FCSTD DOCUMENT  (FreeCAD 1.0R39109 (Git))
Label: 10_shelf_top_assembly
License: All rights reserved
LicenseURL: http://en.wikipedia.org/wiki/All_rights_reserved
objects: App::FeaturePython×25, TechDraw::DrawViewDimension×11, App::Link×9, TechDraw::DrawProjGroupItem×5, Assembly::JointGroup×1, Assembly::AssemblyObject×1, TechDraw::DrawSVGTemplate×1, TechDraw::DrawProjGroup×1, TechDraw::DrawPage×1
note: 17 computed .brp shape members not serialized (recipe doc carries the construction recipe); baked Part::Feature solids carry a one-line shape summary decoded from their .brp
EXTERNAL_REF file=12_shelf_top_down.FCStd obj=Body
EXTERNAL_REF file=13_shelf_sides_and_middle.FCStd obj=Body
EXTERNAL_REF file=14_shelf_trays.FCStd obj=Body

FEATURE [App::Link] Body
  LinkedObject = -> <external 12_shelf_top_down.FCStd>#Body
FEATURE [App::FeaturePython] GroundedJoint  # Assembly grounded joint (typed FeaturePython)
  ObjectToGround = -> Body
FEATURE [App::Link] Body001
  LinkPlacement = pos=(-4.124e-13,4.349e-13,900) rot=(0,1,0;3.14159rad)
  LinkedObject = -> <external 12_shelf_top_down.FCStd>#Body
  Placement = pos=(-4.124e-13,4.349e-13,900) rot=(0,1,0;3.14159rad)
FEATURE [App::Link] Body002
  LinkPlacement = pos=(-597,2.282e-13,450) rot=(0,1,0;4.71239rad)
  LinkedObject = -> <external 13_shelf_sides_and_middle.FCStd>#Body
  Placement = pos=(-597,2.282e-13,450) rot=(0,1,0;4.71239rad)
FEATURE [App::Link] Body003
  LinkPlacement = pos=(615,9.28e-14,450) rot=(0,1,0;4.71239rad)
  LinkedObject = -> <external 13_shelf_sides_and_middle.FCStd>#Body
  Placement = pos=(615,9.28e-14,450) rot=(0,1,0;4.71239rad)
FEATURE [App::Link] Body004
  LinkPlacement = pos=(-9,1.041e-13,450) rot=(0,1,0;1.5708rad)
  LinkedObject = -> <external 13_shelf_sides_and_middle.FCStd>#Body
  Placement = pos=(-9,1.041e-13,450) rot=(0,1,0;1.5708rad)
FEATURE [App::FeaturePython] Joint  label="Distance"  # Assembly joint (typed FeaturePython)
  Activated = true
  AngleMax = 0
  AngleMin = 0
  Detach1 = false
  Detach2 = false
  Distance = 0
  Distance2 = 0
  EnableAngleMax = false
  EnableAngleMin = false
  EnableLengthMax = false
  EnableLengthMin = false
  JointType = 5 (Distance)
  LengthMax = 0
  LengthMin = 0
  Placement1 = pos=(-432,4e-16,9) rot=(0.57735,0.57735,-0.57735;4.18879rad)
  Placement2 = pos=(-4e-15,-5.5e-15,18) rot=(0,0,1;0rad)
  Reference1 = -> Assembly [Body002.Face4,Body002.Face4]
  Reference2 = -> Assembly [Body.Face6,Body.Vertex8]
FEATURE [App::FeaturePython] Joint001  label="Distance001"  # Assembly joint (typed FeaturePython)
  Activated = true
  AngleMax = 0
  AngleMin = 0
  Detach1 = false
  Detach2 = false
  Distance = 0
  Distance2 = 0
  EnableAngleMax = false
  EnableAngleMin = false
  EnableLengthMax = false
  EnableLengthMin = false
  JointType = 5 (Distance)
  LengthMax = 0
  LengthMin = 0
  Placement1 = pos=(0,-2.6e-15,18) rot=(0,0,1;0rad)
  Placement2 = pos=(-615,1.3e-15,9) rot=(-0.57735,-0.57735,0.57735;2.0944rad)
  Reference1 = -> Assembly [Body002.Face6,Body002.Vertex2]
  Reference2 = -> Assembly [Body.Face4,Body.Face4]
FEATURE [App::FeaturePython] Joint002  label="Distance002"  # Assembly joint (typed FeaturePython)
  Activated = true
  AngleMax = 0
  AngleMin = 0
  Detach1 = false
  Detach2 = false
  Distance = 0
  Distance2 = 0
  EnableAngleMax = false
  EnableAngleMin = false
  EnableLengthMax = false
  EnableLengthMin = false
  JointType = 5 (Distance)
  LengthMax = 0
  LengthMin = 0
  Placement1 = pos=(0,87.5,9) rot=(-1,0,0;1.5708rad)
  Placement2 = pos=(6.2e-15,87.5,9) rot=(-1,0,0;1.5708rad)
  Reference1 = -> Assembly [Body002.Face1,Body002.Vertex1]
  Reference2 = -> Assembly [Body.Face1,Body.Vertex1]
FEATURE [App::FeaturePython] Joint003  label="Distance003"  # Assembly joint (typed FeaturePython)
  Activated = true
  AngleMax = 0
  AngleMin = 0
  Detach1 = false
  Detach2 = false
  Distance = 0
  Distance2 = 0
  EnableAngleMax = false
  EnableAngleMin = false
  EnableLengthMax = false
  EnableLengthMin = false
  JointType = 5 (Distance)
  LengthMax = 0
  LengthMin = 0
  Placement1 = pos=(-432,-1.2e-15,9) rot=(0.57735,0.57735,-0.57735;4.18879rad)
  Placement2 = pos=(-4e-15,-5.5e-15,18) rot=(0,0,1;0rad)
  Reference1 = -> Assembly [Body003.Face4,Body003.Face4]
  Reference2 = -> Assembly [Body.Face6,Body.Vertex4]
FEATURE [App::FeaturePython] Joint004  label="Distance004"  # Assembly joint (typed FeaturePython)
  Activated = true
  AngleMax = 0
  AngleMin = 0
  Detach1 = false
  Detach2 = false
  Distance = 0
  Distance2 = 0
  EnableAngleMax = false
  EnableAngleMin = false
  EnableLengthMax = false
  EnableLengthMin = false
  JointType = 5 (Distance)
  LengthMax = 0
  LengthMin = 0
  Placement1 = pos=(0,-87.5,9) rot=(0,-0.707107,0.707107;3.14159rad)
  Placement2 = pos=(-6.2e-15,-87.5,9) rot=(0,-0.707107,0.707107;3.14159rad)
  Reference1 = -> Assembly [Body003.Face3,Body003.Vertex8]
  Reference2 = -> Assembly [Body.Face3,Body.Vertex5]
FEATURE [App::FeaturePython] Joint005  label="Distance005"  # Assembly joint (typed FeaturePython)
  Activated = true
  AngleMax = 0
  AngleMin = 0
  Detach1 = false
  Detach2 = false
  Distance = 0
  Distance2 = 0
  EnableAngleMax = false
  EnableAngleMin = false
  EnableLengthMax = false
  EnableLengthMin = false
  JointType = 5 (Distance)
  LengthMax = 0
  LengthMin = 0
  Placement1 = pos=(0,-6.3e-15,0) rot=(0,0,1;0rad)
  Placement2 = pos=(615,-1.3e-15,9) rot=(0.57735,-0.57735,0.57735;4.18879rad)
  Reference1 = -> Assembly [Body003.Face5,Body003.Vertex7]
  Reference2 = -> Assembly [Body.Face2,Body.Face2]
FEATURE [App::FeaturePython] Joint006  label="Distance006"  # Assembly joint (typed FeaturePython)
  Activated = true
  AngleMax = 0
  AngleMin = 0
  Detach1 = false
  Detach2 = false
  Distance = 0
  Distance2 = 0
  EnableAngleMax = false
  EnableAngleMin = false
  EnableLengthMax = false
  EnableLengthMin = false
  JointType = 5 (Distance)
  LengthMax = 0
  LengthMin = 0
  Placement1 = pos=(432,-1.5e-15,9) rot=(-0.57735,0.57735,-0.57735;2.0944rad)
  Placement2 = pos=(-4e-15,-5.5e-15,18) rot=(0,0,1;0rad)
  Reference1 = -> Assembly [Body004.Face2,Body004.Face2]
  Reference2 = -> Assembly [Body.Face6,Body.Vertex4]
FEATURE [App::FeaturePython] Joint007  label="Distance007"  # Assembly joint (typed FeaturePython)
  Activated = true
  AngleMax = 0
  AngleMin = 0
  Detach1 = false
  Detach2 = false
  Distance = 0
  Distance2 = 0
  EnableAngleMax = false
  EnableAngleMin = false
  EnableLengthMax = false
  EnableLengthMin = false
  JointType = 5 (Distance)
  LengthMax = 0
  LengthMin = 0
  Placement1 = pos=(0,-87.5,9) rot=(0,-0.707107,0.707107;3.14159rad)
  Placement2 = pos=(-6.2e-15,-87.5,9) rot=(0,-0.707107,0.707107;3.14159rad)
  Reference1 = -> Assembly [Body004.Face3,Body004.Vertex6]
  Reference2 = -> Assembly [Body.Face3,Body.Face3]
FEATURE [App::FeaturePython] Joint008  label="Distance008"  # Assembly joint (typed FeaturePython)
  Activated = true
  AngleMax = 0
  AngleMin = 0
  Detach1 = false
  Detach2 = false
  Distance = -588
  Distance2 = 0
  EnableAngleMax = false
  EnableAngleMin = false
  EnableLengthMax = false
  EnableLengthMin = false
  JointType = 5 (Distance)
  LengthMax = 0
  LengthMin = 0
  Placement1 = pos=(0,-2.6e-15,0) rot=(0,0,1;0rad)
  Placement2 = pos=(0,-3.3e-15,0) rot=(0,0,1;0rad)
  Reference1 = -> Assembly [Body002.Face5,Body002.Face5]
  Reference2 = -> Assembly [Body004.Face5,Body004.Face5]
FEATURE [App::FeaturePython] Joint009  label="Distance009"  # Assembly joint (typed FeaturePython)
  Activated = true
  AngleMax = 0
  AngleMin = 0
  Detach1 = false
  Detach2 = false
  Distance = 0
  Distance2 = 0
  EnableAngleMax = false
  EnableAngleMin = false
  EnableLengthMax = false
  EnableLengthMin = false
  JointType = 5 (Distance)
  LengthMax = 0
  LengthMin = 0
  Placement1 = pos=(432,-4e-16,9) rot=(-0.57735,0.57735,-0.57735;2.0944rad)
  Placement2 = pos=(1.04e-14,-3.2e-15,18) rot=(0,0,1;0rad)
  Reference1 = -> Assembly [Body003.Face2,Body003.Vertex5]
  Reference2 = -> Assembly [Body001.Face6,Body001.Face6]
FEATURE [App::FeaturePython] Joint010  label="Distance010"  # Assembly joint (typed FeaturePython)
  Activated = true
  AngleMax = 0
  AngleMin = 0
  Detach1 = false
  Detach2 = false
  Distance = 0
  Distance2 = 0
  EnableAngleMax = false
  EnableAngleMin = false
  EnableLengthMax = false
  EnableLengthMin = false
  JointType = 5 (Distance)
  LengthMax = 0
  LengthMin = 0
  Placement1 = pos=(615,1.5e-15,9) rot=(-0.57735,0.57735,-0.57735;2.0944rad)
  Placement2 = pos=(0,-2.6e-15,18) rot=(0,0,1;0rad)
  Reference1 = -> Assembly [Body001.Face2,Body001.Vertex4]
  Reference2 = -> Assembly [Body002.Face6,Body002.Vertex6]
FEATURE [App::FeaturePython] Joint011  label="Distance011"  # Assembly joint (typed FeaturePython)
  Activated = true
  AngleMax = 0
  AngleMin = 0
  Detach1 = false
  Detach2 = false
  Distance = 0
  Distance2 = 0
  EnableAngleMax = false
  EnableAngleMin = false
  EnableLengthMax = false
  EnableLengthMin = false
  JointType = 5 (Distance)
  LengthMax = 0
  LengthMin = 0
  Placement1 = pos=(-7.8e-15,-87.5,9) rot=(0,-0.707107,0.707107;3.14159rad)
  Placement2 = pos=(0,-87.5,9) rot=(0,-0.707107,0.707107;3.14159rad)
  Reference1 = -> Assembly [Body001.Face3,Body001.Vertex6]
  Reference2 = -> Assembly [Body002.Face3,Body002.Vertex6]
FEATURE [App::Link] Body005
  LinkPlacement = pos=(-303,2.659e-13,294) rot=(0,0,1;3.14159rad)
  LinkedObject = -> <external 14_shelf_trays.FCStd>#Body
  Placement = pos=(-303,2.659e-13,294) rot=(0,0,1;3.14159rad)
FEATURE [App::Link] Body006
  LinkPlacement = pos=(-303,3.633e-13,588) rot=(0,0,1;3.14159rad)
  LinkedObject = -> <external 14_shelf_trays.FCStd>#Body
  Placement = pos=(-303,3.633e-13,588) rot=(0,0,1;3.14159rad)
FEATURE [App::Link] Body007
  LinkPlacement = pos=(303,1.38e-13,294) rot=(0,0,1;3.14159rad)
  LinkedObject = -> <external 14_shelf_trays.FCStd>#Body
  Placement = pos=(303,1.38e-13,294) rot=(0,0,1;3.14159rad)
FEATURE [App::Link] Body008
  LinkPlacement = pos=(303,2.92e-13,588) rot=(0,0,1;3.14159rad)
  LinkedObject = -> <external 14_shelf_trays.FCStd>#Body
  Placement = pos=(303,2.92e-13,588) rot=(0,0,1;3.14159rad)
FEATURE [App::FeaturePython] Joint012  label="Tray1"  # Assembly joint (typed FeaturePython)
  Activated = true
  AngleMax = 0
  AngleMin = 0
  Detach1 = false
  Detach2 = false
  Distance = 276
  Distance2 = 0
  EnableAngleMax = false
  EnableAngleMin = false
  EnableLengthMax = false
  EnableLengthMin = false
  JointType = 5 (Distance)
  LengthMax = 0
  LengthMin = 0
  Placement1 = pos=(0,-3.8e-15,18) rot=(0,0,1;0rad)
  Placement2 = pos=(1.04e-14,-3.2e-15,18) rot=(0,0,1;0rad)
  Reference1 = -> Assembly [Body008.Face6,Body008.Face6]
  Reference2 = -> Assembly [Body001.Face6,Body001.Vertex4]
FEATURE [App::FeaturePython] Joint013  label="Distance013"  # Assembly joint (typed FeaturePython)
  Activated = true
  AngleMax = 0
  AngleMin = 0
  Detach1 = false
  Detach2 = false
  Distance = 0
  Distance2 = 0
  EnableAngleMax = false
  EnableAngleMin = false
  EnableLengthMax = false
  EnableLengthMin = false
  JointType = 5 (Distance)
  LengthMax = 0
  LengthMin = 0
  Placement1 = pos=(0,-6.3e-15,18) rot=(0,0,1;0rad)
  Placement2 = pos=(-294,2.2e-15,9) rot=(-0.57735,-0.57735,0.57735;2.0944rad)
  Reference1 = -> Assembly [Body003.Face6,Body003.Vertex6]
  Reference2 = -> Assembly [Body008.Face4,Body008.Vertex1]
FEATURE [App::FeaturePython] Joint014  label="Distance014"  # Assembly joint (typed FeaturePython)
  Activated = true
  AngleMax = 0
  AngleMin = 0
  Detach1 = false
  Detach2 = false
  Distance = 0
  Distance2 = 0
  EnableAngleMax = false
  EnableAngleMin = false
  EnableLengthMax = false
  EnableLengthMin = false
  JointType = 5 (Distance)
  LengthMax = 0
  LengthMin = 0
  Placement1 = pos=(-7.8e-15,-87.5,9) rot=(0,-0.707107,0.707107;3.14159rad)
  Placement2 = pos=(0,87.5,9) rot=(-1,0,0;1.5708rad)
  Reference1 = -> Assembly [Body001.Face3,Body001.Vertex8]
  Reference2 = -> Assembly [Body008.Face1,Body008.Face1]
FEATURE [App::FeaturePython] Joint015  label="Tray2"  # Assembly joint (typed FeaturePython)
  Activated = true
  AngleMax = 0
  AngleMin = 0
  Detach1 = false
  Detach2 = false
  Distance = 276
  Distance2 = 0
  EnableAngleMax = false
  EnableAngleMin = false
  EnableLengthMax = false
  EnableLengthMin = false
  JointType = 5 (Distance)
  LengthMax = 0
  LengthMin = 0
  Placement1 = pos=(0,-3.9e-15,18) rot=(0,0,1;0rad)
  Placement2 = pos=(0,-3.8e-15,0) rot=(0,0,1;0rad)
  Reference1 = -> Assembly [Body007.Face6,Body007.Face6]
  Reference2 = -> Assembly [Body008.Face5,Body008.Vertex5]
FEATURE [App::FeaturePython] Joint016  label="Distance016"  # Assembly joint (typed FeaturePython)
  Activated = true
  AngleMax = 0
  AngleMin = 0
  Detach1 = false
  Detach2 = false
  Distance = 0
  Distance2 = 0
  EnableAngleMax = false
  EnableAngleMin = false
  EnableLengthMax = false
  EnableLengthMin = false
  JointType = 5 (Distance)
  LengthMax = 0
  LengthMin = 0
  Placement1 = pos=(-294,1e-15,9) rot=(-0.57735,-0.57735,0.57735;2.0944rad)
  Placement2 = pos=(0,-6.3e-15,18) rot=(0,0,1;0rad)
  Reference1 = -> Assembly [Body007.Face4,Body007.Vertex2]
  Reference2 = -> Assembly [Body003.Face6,Body003.Face6]
FEATURE [App::FeaturePython] Joint017  label="Distance017"  # Assembly joint (typed FeaturePython)
  Activated = true
  AngleMax = 0
  AngleMin = 0
  Detach1 = false
  Detach2 = false
  Distance = 0
  Distance2 = 0
  EnableAngleMax = false
  EnableAngleMin = false
  EnableLengthMax = false
  EnableLengthMin = false
  JointType = 5 (Distance)
  LengthMax = 0
  LengthMin = 0
  Placement1 = pos=(0,87.5,9) rot=(-1,0,0;1.5708rad)
  Placement2 = pos=(0,-87.5,9) rot=(0,-0.707107,0.707107;3.14159rad)
  Reference1 = -> Assembly [Body007.Face1,Body007.Vertex2]
  Reference2 = -> Assembly [Body003.Face3,Body003.Face3]
FEATURE [App::FeaturePython] Joint018  label="tray3"  # Assembly joint (typed FeaturePython)
  Activated = true
  AngleMax = 0
  AngleMin = 0
  Detach1 = false
  Detach2 = false
  Distance = 276
  Distance2 = 0
  EnableAngleMax = false
  EnableAngleMin = false
  EnableLengthMax = false
  EnableLengthMin = false
  JointType = 5 (Distance)
  LengthMax = 0
  LengthMin = 0
  Placement1 = pos=(0,2.4e-15,18) rot=(0,0,1;0rad)
  Placement2 = pos=(1.04e-14,-3.2e-15,18) rot=(0,0,1;0rad)
  Reference1 = -> Assembly [Body006.Face6,Body006.Vertex2]
  Reference2 = -> Assembly [Body001.Face6,Body001.Face6]
FEATURE [App::FeaturePython] Joint019  label="Distance019"  # Assembly joint (typed FeaturePython)
  Activated = true
  AngleMax = 0
  AngleMin = 0
  Detach1 = false
  Detach2 = false
  Distance = 0
  Distance2 = 0
  EnableAngleMax = false
  EnableAngleMin = false
  EnableLengthMax = false
  EnableLengthMin = false
  JointType = 5 (Distance)
  LengthMax = 0
  LengthMin = 0
  Placement1 = pos=(0,87.5,9) rot=(-1,0,0;1.5708rad)
  Placement2 = pos=(-7.8e-15,-87.5,9) rot=(0,-0.707107,0.707107;3.14159rad)
  Reference1 = -> Assembly [Body006.Face1,Body006.Vertex4]
  Reference2 = -> Assembly [Body001.Face3,Body001.Face3]
FEATURE [App::FeaturePython] Joint020  label="Distance020"  # Assembly joint (typed FeaturePython)
  Activated = true
  AngleMax = 0
  AngleMin = 0
  Detach1 = false
  Detach2 = false
  Distance = 0
  Distance2 = 0
  EnableAngleMax = false
  EnableAngleMin = false
  EnableLengthMax = false
  EnableLengthMin = false
  JointType = 5 (Distance)
  LengthMax = 0
  LengthMin = 0
  Placement1 = pos=(0,-2.6e-15,0) rot=(0,0,1;0rad)
  Placement2 = pos=(294,1.1e-15,9) rot=(-0.57735,0.57735,-0.57735;2.0944rad)
  Reference1 = -> Assembly [Body002.Face5,Body002.Vertex3]
  Reference2 = -> Assembly [Body006.Face2,Body006.Face2]
FEATURE [App::FeaturePython] Joint021  label="tray4"  # Assembly joint (typed FeaturePython)
  Activated = true
  AngleMax = 0
  AngleMin = 0
  Detach1 = false
  Detach2 = false
  Distance = 276
  Distance2 = 0
  EnableAngleMax = false
  EnableAngleMin = false
  EnableLengthMax = false
  EnableLengthMin = false
  JointType = 5 (Distance)
  LengthMax = 0
  LengthMin = 0
  Placement1 = pos=(0,-4.5e-15,18) rot=(0,0,1;0rad)
  Placement2 = pos=(0,-5.2e-15,0) rot=(0,0,1;0rad)
  Reference1 = -> Assembly [Body005.Face6,Body005.Face6]
  Reference2 = -> Assembly [Body006.Face5,Body006.Face5]
FEATURE [App::FeaturePython] Joint022  label="Distance021"  # Assembly joint (typed FeaturePython)
  Activated = true
  AngleMax = 0
  AngleMin = 0
  Detach1 = false
  Detach2 = false
  Distance = 0
  Distance2 = 0
  EnableAngleMax = false
  EnableAngleMin = false
  EnableLengthMax = false
  EnableLengthMin = false
  JointType = 5 (Distance)
  LengthMax = 0
  LengthMin = 0
  Placement1 = pos=(0,-87.5,9) rot=(0,-0.707107,0.707107;3.14159rad)
  Placement2 = pos=(0,87.5,9) rot=(-1,0,0;1.5708rad)
  Reference1 = -> Assembly [Body002.Face3,Body002.Face3]
  Reference2 = -> Assembly [Body005.Face1,Body005.Vertex4]
FEATURE [App::FeaturePython] Joint023  label="Distance022"  # Assembly joint (typed FeaturePython)
  Activated = true
  AngleMax = 0
  AngleMin = 0
  Detach1 = false
  Detach2 = false
  Distance = 0
  Distance2 = 0
  EnableAngleMax = false
  EnableAngleMin = false
  EnableLengthMax = false
  EnableLengthMin = false
  JointType = 5 (Distance)
  LengthMax = 0
  LengthMin = 0
  Placement1 = pos=(294,9e-16,9) rot=(-0.57735,0.57735,-0.57735;2.0944rad)
  Placement2 = pos=(0,-2.6e-15,0) rot=(0,0,1;0rad)
  Reference1 = -> Assembly [Body005.Face2,Body005.Vertex3]
  Reference2 = -> Assembly [Body002.Face5,Body002.Face5]
FEATURE [Assembly::JointGroup] Joints
  Group = -> [GroundedJoint,Joint,Joint001,Joint002,Joint003,Joint004,Joint005,Joint006,Joint007,Joint008,Joint009,Joint010,Joint011,Joint012,Joint013,Joint014,Joint015,Joint016,Joint017,Joint018,Joint019,Joint020,Joint021,Joint022,Joint023]
FEATURE [Assembly::AssemblyObject] Assembly
  Group = -> [Joints,Body,GroundedJoint,Body001,Body002,Body003,Body004,Joint,Joint001,Joint002,Joint003,Joint004,Joint005,Joint006,Joint007,Joint008,Joint009,Joint010,Joint011,Body005,Body006,Body007,Body008,Joint012,Joint013,Joint014,Joint015,Joint016,Joint017,Joint018,Joint019,Joint020,Joint021,Joint022,Joint023]
  Origin = -> Origin
  Type = Assembly
FEATURE [TechDraw::DrawSVGTemplate] Template
  EditableTexts = AuthorName=Matthias Mosimann; CheckDate=CHECK DATE; CreationDate=21/07/2025; DrawingNumber=NUMBER; FC-Scale=1 : 10; FC-Title=Regal oben; SheetNumber=1/2; Subtitle=Alle Dicken 18mm Buche keilverzinkt; SupervisorName=SUPERVISOR NAME; Weight=N/A
  Height = 297
  Orientation = 1
  Template = C:/Program Files/FreeCAD 1.0/data/Mod/TechDraw/Templates/A3_Landscape_TD.svg
  Width = 420
FEATURE [TechDraw::DrawProjGroupItem] View  label="Front"
  CoarseView = false
  Direction = (0,-1,0)
  Focus = 100
  HardHidden = false
  IsoCount = 0
  IsoHidden = false
  IsoVisible = false
  LockPosition = true
  Perspective = false
  Rotation = 0
  RotationVector = (1,0,0)
  Scale = 0.1
  ScaleType = 2
  ScrubCount = 1
  SeamHidden = false
  SeamVisible = true
  SmoothHidden = false
  SmoothVisible = true
  Source = -> [Assembly]
  Type = 0
  X = 0
  XDirection = (1,0,0)
  Y = 0
FEATURE [TechDraw::DrawProjGroupItem] ProjItem  label="Left"
  CoarseView = false
  Direction = (-1,-1e-16,0)
  Focus = 100
  HardHidden = false
  IsoCount = 0
  IsoHidden = false
  IsoVisible = false
  LockPosition = false
  Perspective = false
  Rotation = 0
  RotationVector = (1,0,0)
  ScaleType = 0
  ScrubCount = 1
  SeamHidden = false
  SeamVisible = true
  SmoothHidden = false
  SmoothVisible = true
  Source = -> [Assembly]
  Type = 1
  X = 85.25
  XDirection = (1e-16,-1,0)
  Y = 0
FEATURE [TechDraw::DrawProjGroupItem] ProjItem001  label="Right"
  CoarseView = false
  Direction = (1,-1e-16,0)
  Focus = 100
  HardHidden = false
  IsoCount = 0
  IsoHidden = false
  IsoVisible = false
  LockPosition = false
  Perspective = false
  Rotation = 0
  RotationVector = (1,0,0)
  ScaleType = 0
  ScrubCount = 1
  SeamHidden = false
  SeamVisible = true
  SmoothHidden = false
  SmoothVisible = true
  Source = -> [Assembly]
  Type = 2
  X = -85.25
  XDirection = (1e-16,1,0)
  Y = 0
FEATURE [TechDraw::DrawProjGroupItem] ProjItem002  label="Top"
  CoarseView = false
  Direction = (0,0,1)
  Focus = 100
  HardHidden = false
  IsoCount = 0
  IsoHidden = false
  IsoVisible = false
  LockPosition = false
  Perspective = false
  Rotation = 0
  RotationVector = (1,0,0)
  ScaleType = 0
  ScrubCount = 1
  SeamHidden = false
  SeamVisible = true
  SmoothHidden = false
  SmoothVisible = true
  Source = -> [Assembly]
  Type = 4
  X = 0
  XDirection = (1,0,0)
  Y = -68.75
FEATURE [TechDraw::DrawProjGroup] ProjGroup
  Anchor = -> View
  AutoDistribute = true
  LockPosition = false
  ProjectionType = 0
  Rotation = 0
  Scale = 0.1
  ScaleType = 2
  Source = -> [Assembly]
  Views = -> [View,ProjItem,ProjItem001,ProjItem002]
  X = 179.598
  Y = 208.711
  spacingX = 15
  spacingY = 15
FEATURE [TechDraw::DrawViewDimension] Dimension001
  AngleOverride = false
  Arbitrary = false
  ArbitraryTolerances = false
  BoxCorners = (2) [(-8.75,-45,0),(8.75,45,0)]
  EqualTolerance = true
  ExtensionAngle = 0
  FormatSpec = %.2w
  FormatSpecOverTolerance = %+.2w
  FormatSpecUnderTolerance = %+.2w
  Inverted = false
  LineAngle = 0
  LockPosition = false
  MeasureType = 1
  OverTolerance = 0
  References2D = -> [ProjItem001]
  Rotation = 0
  ScaleType = 0
  TheoreticalExact = false
  Type = 1
  UnderTolerance = 0
  X = 0
  Y = 63.1902
FEATURE [TechDraw::DrawViewDimension] Dimension002
  AngleOverride = false
  Arbitrary = false
  ArbitraryTolerances = false
  BoxCorners = (2) [(-8.75,-45,0),(8.75,45,0)]
  EqualTolerance = true
  ExtensionAngle = 0
  FormatSpec = %.2w
  FormatSpecOverTolerance = %+.2w
  FormatSpecUnderTolerance = %+.2w
  Inverted = false
  LineAngle = 0
  LockPosition = false
  MeasureType = 1
  OverTolerance = 0
  References2D = -> [ProjItem001]
  Rotation = 0
  ScaleType = 0
  TheoreticalExact = false
  Type = 0
  UnderTolerance = 0
  X = -23.6689
  Y = 0
FEATURE [TechDraw::DrawViewDimension] Dimension003
  AngleOverride = false
  Arbitrary = false
  ArbitraryTolerances = false
  BoxCorners = (2) [(-61.5,-45,0),(61.5,45,0)]
  EqualTolerance = true
  ExtensionAngle = 0
  FormatSpec = %.2w
  FormatSpecOverTolerance = %+.2w
  FormatSpecUnderTolerance = %+.2w
  Inverted = false
  LineAngle = 0
  LockPosition = false
  MeasureType = 1
  OverTolerance = 0
  References2D = -> [View]
  Rotation = 0
  ScaleType = 0
  TheoreticalExact = false
  Type = 0
  UnderTolerance = 0
  X = -80.2278
  Y = 24.7431
FEATURE [TechDraw::DrawViewDimension] Dimension004
  AngleOverride = false
  Arbitrary = false
  ArbitraryTolerances = false
  BoxCorners = (2) [(-61.5,-45,0),(61.5,45,0)]
  EqualTolerance = true
  ExtensionAngle = 0
  FormatSpec = %.2w
  FormatSpecOverTolerance = %+.2w
  FormatSpecUnderTolerance = %+.2w
  Inverted = false
  LineAngle = 0
  LockPosition = false
  MeasureType = 1
  OverTolerance = 0
  References2D = -> [View]
  Rotation = 0
  ScaleType = 0
  TheoreticalExact = false
  Type = 0
  UnderTolerance = 0
  X = -80.2278
  Y = -5.13293
FEATURE [TechDraw::DrawViewDimension] Dimension005
  AngleOverride = false
  Arbitrary = false
  ArbitraryTolerances = false
  BoxCorners = (2) [(-61.5,-45,0),(61.5,45,0)]
  EqualTolerance = true
  ExtensionAngle = 0
  FormatSpec = %.2w
  FormatSpecOverTolerance = %+.2w
  FormatSpecUnderTolerance = %+.2w
  Inverted = false
  LineAngle = 0
  LockPosition = false
  MeasureType = 1
  OverTolerance = 0
  References2D = -> [View]
  Rotation = 0
  ScaleType = 0
  TheoreticalExact = false
  Type = 0
  UnderTolerance = 0
  X = -80.2278
  Y = -33.0319
FEATURE [TechDraw::DrawViewDimension] Dimension006
  AngleOverride = false
  Arbitrary = false
  ArbitraryTolerances = false
  BoxCorners = (2) [(-8.75,-45,0),(8.75,45,0)]
  EqualTolerance = true
  ExtensionAngle = 0
  FormatSpec = %.2w
  FormatSpecOverTolerance = %+.2w
  FormatSpecUnderTolerance = %+.2w
  Inverted = false
  LineAngle = 0
  LockPosition = false
  MeasureType = 1
  OverTolerance = 0
  References2D = -> [ProjItem001]
  Rotation = 0
  ScaleType = 0
  TheoreticalExact = false
  Type = 2
  UnderTolerance = 0
  X = -16.6689
  Y = 0
FEATURE [TechDraw::DrawViewDimension] Dimension007
  AngleOverride = false
  Arbitrary = false
  ArbitraryTolerances = false
  BoxCorners = (2) [(-8.75,-45,0),(8.75,45,0)]
  EqualTolerance = true
  ExtensionAngle = 0
  FormatSpec = %.2w
  FormatSpecOverTolerance = %+.2w
  FormatSpecUnderTolerance = %+.2w
  Inverted = false
  LineAngle = 0
  LockPosition = false
  MeasureType = 1
  OverTolerance = 0
  References2D = -> [ProjItem]
  Rotation = 0
  ScaleType = 0
  TheoreticalExact = false
  Type = 2
  UnderTolerance = 0
  X = 18.0927
  Y = 39.4399
FEATURE [TechDraw::DrawViewDimension] Dimension008
  AngleOverride = false
  Arbitrary = false
  ArbitraryTolerances = false
  BoxCorners = (2) [(-8.75,-45,0),(8.75,45,0)]
  EqualTolerance = true
  ExtensionAngle = 0
  FormatSpec = %.2w
  FormatSpecOverTolerance = %+.2w
  FormatSpecUnderTolerance = %+.2w
  Inverted = false
  LineAngle = 0
  LockPosition = false
  MeasureType = 1
  OverTolerance = 0
  References2D = -> [ProjItem]
  Rotation = 0
  ScaleType = 0
  TheoreticalExact = false
  Type = 1
  UnderTolerance = 0
  X = 0
  Y = 65.9025
FEATURE [TechDraw::DrawProjGroupItem] View001
  CoarseView = false
  Direction = (0.57735,-0.57735,0.57735)
  Focus = 100
  HardHidden = false
  IsoCount = 0
  IsoHidden = false
  IsoVisible = false
  LockPosition = false
  Perspective = false
  Rotation = 0
  RotationVector = (1,0,0)
  Scale = 0.1
  ScaleType = 2
  ScrubCount = 1
  SeamHidden = false
  SeamVisible = true
  SmoothHidden = false
  SmoothVisible = true
  Source = -> [Assembly]
  Type = 0
  X = 344.673
  XDirection = (0.707107,0.707107,0)
  Y = 156.038
FEATURE [TechDraw::DrawViewDimension] Dimension
  AngleOverride = false
  Arbitrary = false
  ArbitraryTolerances = false
  BoxCorners = (2) [(-61.5,-8.75,0),(61.5,8.75,0)]
  EqualTolerance = true
  ExtensionAngle = 0
  FormatSpec = %.2w
  FormatSpecOverTolerance = %+.2w
  FormatSpecUnderTolerance = %+.2w
  Inverted = false
  LineAngle = 0
  LockPosition = false
  MeasureType = 1
  OverTolerance = 0
  References2D = -> [ProjItem002]
  Rotation = 0
  ScaleType = 0
  TheoreticalExact = false
  Type = 1
  UnderTolerance = 0
  X = 0
  Y = 20.3647
FEATURE [TechDraw::DrawViewDimension] Dimension009
  AngleOverride = false
  Arbitrary = false
  ArbitraryTolerances = false
  BoxCorners = (2) [(-61.5,-45,0),(61.5,45,0)]
  EqualTolerance = true
  ExtensionAngle = 0
  FormatSpec = %.2w
  FormatSpecOverTolerance = %+.2w
  FormatSpecUnderTolerance = %+.2w
  Inverted = false
  LineAngle = 0
  LockPosition = false
  MeasureType = 1
  OverTolerance = 0
  References2D = -> [View]
  Rotation = 0
  ScaleType = 0
  TheoreticalExact = false
  Type = 0
  UnderTolerance = 0
  X = -30.3
  Y = 65.3418
FEATURE [TechDraw::DrawViewDimension] Dimension010
  AngleOverride = false
  Arbitrary = false
  ArbitraryTolerances = false
  BoxCorners = (2) [(-61.5,-45,0),(61.5,45,0)]
  EqualTolerance = true
  ExtensionAngle = 0
  FormatSpec = %.2w
  FormatSpecOverTolerance = %+.2w
  FormatSpecUnderTolerance = %+.2w
  Inverted = false
  LineAngle = 0
  LockPosition = false
  MeasureType = 1
  OverTolerance = 0
  References2D = -> [View]
  Rotation = 0
  ScaleType = 0
  TheoreticalExact = false
  Type = 0
  UnderTolerance = 0
  X = 30.3
  Y = 65.3418
FEATURE [TechDraw::DrawPage] Page001
  KeepUpdated = true
  NextBalloonIndex = 1
  ProjectionType = 0
  Template = -> Template
  Views = -> [ProjGroup,Dimension001,Dimension002,Dimension003,Dimension004,Dimension005,Dimension006,Dimension007,Dimension008,View001,Dimension,Dimension009,Dimension010]

RESOLVED EXTERNAL PARTS (link-assembly join: the EXTERNAL_REF files above that resolve inside this repo's crawl, each included once):
---- part 12_shelf_top_down.FCStd = doc fcstd_a2ddd8781cf4 ----
FCSTD DOCUMENT  (FreeCAD 1.0R39109 (Git))
Label: 12_shelf_top_down
License: All rights reserved
LicenseURL: http://en.wikipedia.org/wiki/All_rights_reserved
objects: Spreadsheet::Sheet×1, Sketcher::SketchObject×1, PartDesign::Pad×1, PartDesign::Body×1
note: 6 computed .brp shape members not serialized (recipe doc carries the construction recipe); baked Part::Feature solids carry a one-line shape summary decoded from their .brp

FEATURE [Spreadsheet::Sheet] Spreadsheet
  cells = A2='length; B2(length)=1230; A3='width; B3(width)=175; A4='height; B4(height)=18
FEATURE [Sketcher::SketchObject] Sketch
  ArcFitTolerance = 0
  AttachmentSupport = -> [XY_Plane]
  FullyConstrained = true
  MakeInternals = false
  MapMode = 5
  expr: Constraints[11] = Spreadsheet.length
  expr: Constraints[12] = Spreadsheet.width
  sketch-geometry (5):
    g0: LineSegment StartX=-615 StartY=87.5 StartZ=0 EndX=615 EndY=87.5 EndZ=0
    g1: LineSegment StartX=615 StartY=87.5 StartZ=0 EndX=615 EndY=-87.5 EndZ=0
    g2: LineSegment StartX=615 StartY=-87.5 StartZ=0 EndX=-615 EndY=-87.5 EndZ=0
    g3: LineSegment StartX=-615 StartY=-87.5 StartZ=0 EndX=-615 EndY=87.5 EndZ=0
    g4: LineSegment [constr] StartX=-615 StartY=87.5 StartZ=0 EndX=615 EndY=-87.5 EndZ=0
  constraints (13):
    c: Coincident(g0,g1)
    c: Coincident(g1,g2)
    c: Coincident(g2,g3)
    c: Coincident(g3,g0)
    c: Horizontal(g0)
    c: Horizontal(g2)
    c: Vertical(g1)
    c: Vertical(g3)
    c: Coincident(g4,g1)
    c: Coincident(g0,g4)
    c: Symmetric(g0,g1,g-1)
    c: Distance(g0,g0) = 1230
    c: Distance(g0,g2) = 175
FEATURE [PartDesign::Pad] Pad
  Direction = (0,0,1)
  Length = 18
  Length2 = 10
  Profile = -> Sketch
  ReferenceAxis = -> Sketch [N_Axis]
  Suppressed = false
  Type = 0
  expr: Length = Spreadsheet.height
FEATURE [PartDesign::Body] Body
  AllowCompound = false
  Group = -> [Sketch,Pad]
  Origin = -> Origin
  Tip = -> Pad
---- part 13_shelf_sides_and_middle.FCStd = doc fcstd_5c3ea9e0d13c ----
FCSTD DOCUMENT  (FreeCAD 1.0R39109 (Git))
Label: 13_shelf_sides_and_middle
License: All rights reserved
LicenseURL: http://en.wikipedia.org/wiki/All_rights_reserved
objects: Spreadsheet::Sheet×1, Sketcher::SketchObject×1, PartDesign::Pad×1, PartDesign::Body×1
note: 6 computed .brp shape members not serialized (recipe doc carries the construction recipe); baked Part::Feature solids carry a one-line shape summary decoded from their .brp

FEATURE [Spreadsheet::Sheet] Spreadsheet
  cells = A2='length; B2(length)=864; A3='width; B3(width)=175; A4='height; B4(height)=18
FEATURE [Sketcher::SketchObject] Sketch
  ArcFitTolerance = 0
  AttachmentSupport = -> [XY_Plane]
  FullyConstrained = true
  MakeInternals = false
  MapMode = 5
  expr: Constraints[11] = Spreadsheet.length
  expr: Constraints[12] = Spreadsheet.width
  sketch-geometry (5):
    g0: LineSegment StartX=-432 StartY=87.5 StartZ=0 EndX=432 EndY=87.5 EndZ=0
    g1: LineSegment StartX=432 StartY=87.5 StartZ=0 EndX=432 EndY=-87.5 EndZ=0
    g2: LineSegment StartX=432 StartY=-87.5 StartZ=0 EndX=-432 EndY=-87.5 EndZ=0
    g3: LineSegment StartX=-432 StartY=-87.5 StartZ=0 EndX=-432 EndY=87.5 EndZ=0
    g4: LineSegment [constr] StartX=-432 StartY=87.5 StartZ=0 EndX=432 EndY=-87.5 EndZ=0
  constraints (13):
    c: Coincident(g0,g1)
    c: Coincident(g1,g2)
    c: Coincident(g2,g3)
    c: Coincident(g3,g0)
    c: Horizontal(g0)
    c: Horizontal(g2)
    c: Vertical(g1)
    c: Vertical(g3)
    c: Coincident(g4,g1)
    c: Coincident(g0,g4)
    c: Symmetric(g0,g1,g-1)
    c: Distance(g0,g0) = 864
    c: Distance(g0,g2) = 175
FEATURE [PartDesign::Pad] Pad
  Direction = (0,0,1)
  Length = 18
  Length2 = 10
  Profile = -> Sketch
  ReferenceAxis = -> Sketch [N_Axis]
  Suppressed = false
  Type = 0
  expr: Length = Spreadsheet.height
FEATURE [PartDesign::Body] Body
  AllowCompound = false
  Group = -> [Sketch,Pad]
  Origin = -> Origin
  Tip = -> Pad
---- part 14_shelf_trays.FCStd = doc fcstd_74c0f5ad40a8 ----
FCSTD DOCUMENT  (FreeCAD 1.0R39109 (Git))
Label: 14_shelf_trays
License: All rights reserved
LicenseURL: http://en.wikipedia.org/wiki/All_rights_reserved
objects: Spreadsheet::Sheet×1, Sketcher::SketchObject×1, PartDesign::Pad×1, PartDesign::Body×1
note: 6 computed .brp shape members not serialized (recipe doc carries the construction recipe); baked Part::Feature solids carry a one-line shape summary decoded from their .brp

FEATURE [Spreadsheet::Sheet] Spreadsheet
  cells = A2='length; B2(length)=588; A3='width; B3(width)=175; A4='height; B4(height)=18
FEATURE [Sketcher::SketchObject] Sketch
  ArcFitTolerance = 0
  AttachmentSupport = -> [XY_Plane]
  FullyConstrained = true
  MakeInternals = false
  MapMode = 5
  expr: Constraints[11] = Spreadsheet.length
  expr: Constraints[12] = Spreadsheet.width
  sketch-geometry (5):
    g0: LineSegment StartX=-294 StartY=87.5 StartZ=0 EndX=294 EndY=87.5 EndZ=0
    g1: LineSegment StartX=294 StartY=87.5 StartZ=0 EndX=294 EndY=-87.5 EndZ=0
    g2: LineSegment StartX=294 StartY=-87.5 StartZ=0 EndX=-294 EndY=-87.5 EndZ=0
    g3: LineSegment StartX=-294 StartY=-87.5 StartZ=0 EndX=-294 EndY=87.5 EndZ=0
    g4: LineSegment [constr] StartX=-294 StartY=87.5 StartZ=0 EndX=294 EndY=-87.5 EndZ=0
  constraints (13):
    c: Coincident(g0,g1)
    c: Coincident(g1,g2)
    c: Coincident(g2,g3)
    c: Coincident(g3,g0)
    c: Horizontal(g0)
    c: Horizontal(g2)
    c: Vertical(g1)
    c: Vertical(g3)
    c: Coincident(g4,g1)
    c: Coincident(g0,g4)
    c: Symmetric(g0,g1,g-1)
    c: Distance(g0,g0) = 588
    c: Distance(g0,g2) = 175
FEATURE [PartDesign::Pad] Pad
  Direction = (0,0,1)
  Length = 18
  Length2 = 10
  Profile = -> Sketch
  ReferenceAxis = -> Sketch [N_Axis]
  Suppressed = false
  Type = 0
  expr: Length = Spreadsheet.height
FEATURE [PartDesign::Body] Body
  AllowCompound = false
  Group = -> [Sketch,Pad]
  Origin = -> Origin
  Tip = -> Pad
